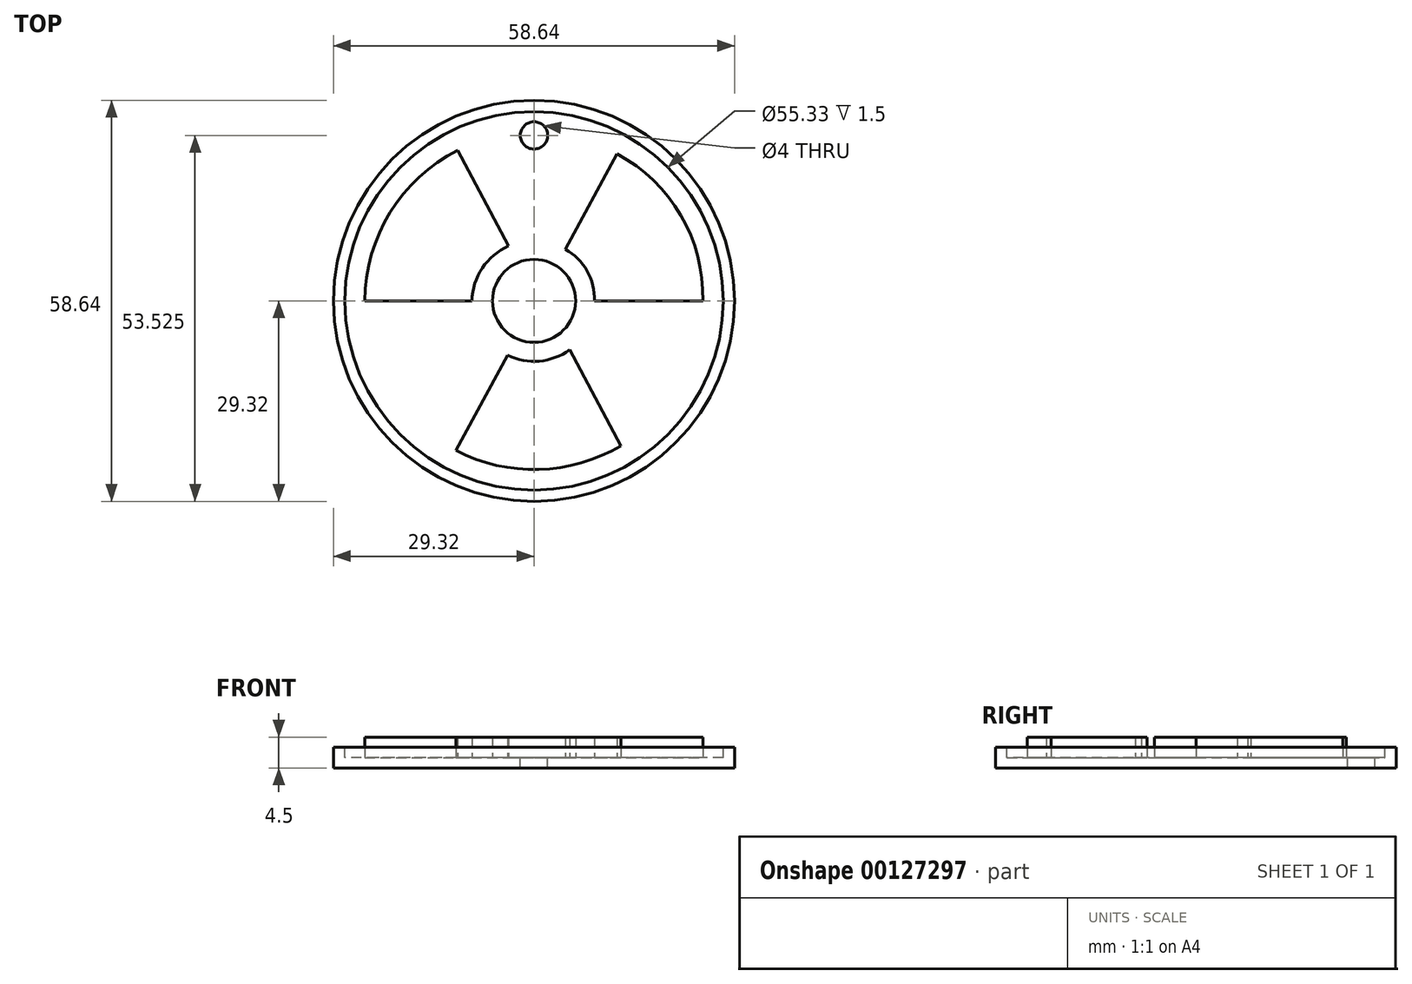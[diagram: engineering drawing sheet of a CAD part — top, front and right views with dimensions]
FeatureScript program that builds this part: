
annotation { "Feature Type Name" : "Feature", "Feature Type Description" : "" }
export const myFeature = defineFeature(function(context is Context, id is Id, definition is map)
    precondition{}
    {
        {
            var Q0;
            Q0=qCreatedBy(makeId("Top.planeOp"),FACE);
            var sketch = newSketch(context, id + "F0", { "sketchPlane" : qUnion([Q0])});
            skCircle(sketch, "E0", {"center": v(0, 0) * mm, "radius": 29.32 * mm});
            skSolve(sketch);
        }
        {
            var Q0;
            Q0=makeQuery(id+"F0.imprint","IMPRINT",FACE,{"disambiguationData":[TD([[makeQuery(id+"F0.imprint","IMPRINT",EDGE,{"derivedFrom":sQuery(id+"F0.wireOp",EDGE,"E0")}),1.0]])]});
            extrude(context, id + "F1", {"entities" : qUnion([Q0]), "depth" : 3 * mm});
        }
        {
            var Q0;
            Q0=makeQuery(id+"F1.opExtrude","CAP_FACE",FACE,{"disambiguationData":[OSD([sQuery(id+"F0.wireOp",EDGE,"E0")])],"isStart":false});
            var sketch = newSketch(context, id + "F2", { "sketchPlane" : qUnion([Q0])});
            skCircle(sketch, "E1", {"center": v(0, 0) * mm, "radius": 27.67 * mm});
            skSolve(sketch);
        }
        {
            var Q0;
            Q0 = qSketchRegion(id + "F2", true);
            extrude(context, id + "F3", {"entities" : qUnion([Q0]), "operationType" : NewBodyOperationType.REMOVE, "oppositeDirection" : true, "depth" : 1.5 * mm});
        }
        {
            var Q0;
            Q0=makeQuery(id+"F3.boolean.opBoolean","COPY",FACE,{"derivedFrom":makeQuery(id+"F3.opExtrude","CAP_FACE",FACE,{"disambiguationData":[OSD([sQuery(id+"F2.wireOp",EDGE,"E1")])],"isStart":false})});
            var sketch = newSketch(context, id + "F4", { "sketchPlane" : qUnion([Q0])});
            skCircle(sketch, "E2", {"center": v(0, 0) * mm, "radius": 6.07 * mm});
            skLineSegment(sketch, "E3", {"start": v(-24.77, 0) * mm, "end": v(-9.1, 0) * mm});
            skLineSegment(sketch, "E4", {"start": v(8.84, 0) * mm, "end": v(24.7, 0) * mm});
            skLineSegment(sketch, "E5", {"start": v(-3.71, 8.02) * mm, "end": v(-11.18, 22.02) * mm});
            skLineSegment(sketch, "E6", {"start": v(12.69, -21.19) * mm, "end": v(5.2, -7.15) * mm});
            skPoint(sketch, "E7", {"position": v(4.58, 7.56) * mm});
            skPoint(sketch, "E8", {"position": v(-3.86, -7.95) * mm});
            skPoint(sketch, "E9", {"position": v(12.16, 21.5) * mm});
            skPoint(sketch, "E10", {"position": v(-11.45, -21.88) * mm});
            skLineSegment(sketch, "E11", {"start": v(-11.45, -21.88) * mm, "end": v(-3.86, -7.95) * mm});
            skLineSegment(sketch, "E12", {"start": v(4.58, 7.56) * mm, "end": v(12.16, 21.5) * mm});
            skArc(sketch, "E13", {"start": v(-11.18, 22.02) * mm, "mid": v(-21.06, 12.9) * mm, "end": v(-24.77, 0) * mm});
            skArc(sketch, "E14", {"start": v(24.7, 0) * mm, "mid": v(21.47, 12.52) * mm, "end": v(12.16, 21.5) * mm});
            skArc(sketch, "E15", {"start": v(-11.45, -21.88) * mm, "mid": v(0.7, -24.66) * mm, "end": v(12.69, -21.19) * mm});
            skArc(sketch, "E16", {"start": v(-3.86, -7.95) * mm, "mid": v(0.78, -8.82) * mm, "end": v(5.2, -7.15) * mm});
            skArc(sketch, "E17", {"start": v(8.84, 0) * mm, "mid": v(7.76, 4.37) * mm, "end": v(4.58, 7.56) * mm});
            skArc(sketch, "E18", {"start": v(-3.71, 8.02) * mm, "mid": v(-7.58, 4.8) * mm, "end": v(-9.1, 0) * mm});
            skSolve(sketch);
        }
        {
            var Q0;
            Q0 = qSketchRegion(id + "F4", true);
            extrude(context, id + "F5", {"entities" : qUnion([Q0]), "operationType" : NewBodyOperationType.ADD, "depth" : 3 * mm});
        }
        {
            var Q0;
            Q0=makeQuery(id+"F3.boolean.opBoolean","COPY",FACE,{"derivedFrom":makeQuery(id+"F3.opExtrude","CAP_FACE",FACE,{"disambiguationData":[OSD([sQuery(id+"F2.wireOp",EDGE,"E1")])],"isStart":false})});
            var sketch = newSketch(context, id + "F6", { "sketchPlane" : qUnion([Q0])});
            skPoint(sketch, "E19", {"position": v(0, 24.2) * mm});
            skSolve(sketch);
        }
        {
            var Q0;
            Q0=sQuery(id+"F6.wireOp",VERTEX,"E19");
            var Q1;
            Q1=makeQuery(id+"F1.opExtrude","SWEPT_BODY",BODY,{"disambiguationData":[OSD([sQuery(id+"F0.wireOp",EDGE,"E0")])]});
            hole(context, id + "F7", {"style" : HoleStyle.SIMPLE, "endStyle" : HoleEndStyle.BLIND, "holeDiameter" : 4 * mm, "holeDepth" : 2 * mm, "locations" : qUnion([Q0]), "scope" : qUnion([Q1])});
        }
    });
